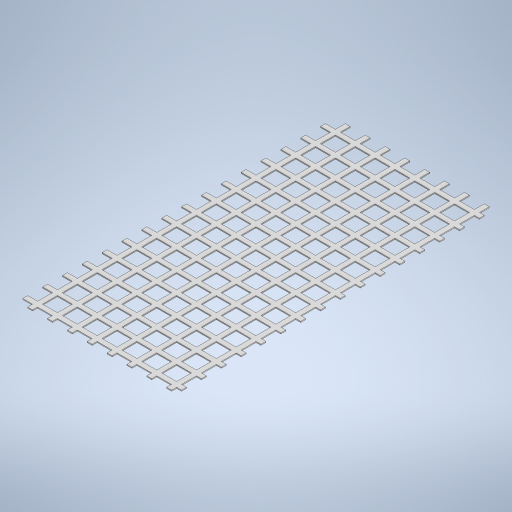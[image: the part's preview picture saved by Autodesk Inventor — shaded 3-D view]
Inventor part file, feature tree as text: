
AUTODESK INVENTOR PART (.ipt)
format: ipt  version: 2023 (Build 270158000, 158)  size: 695,296 bytes
history: native  units: in
note: dims shown in document units (in); Inventor stores cm internally (conversion verified against a paired STEP export)
features: extrude x2, pattern_linear x2, sketch x1
ambient origin geometry x8: Origin, YZ Plane, XZ Plane, XY Plane, X Axis, Y Axis, Z Axis, Center Point
bodies: Solid1 (feature_tree)
feature tree (5):
  sketch  "Sketch1"  dims[d0=54.0in d1=54.0in d2=1.0in d3=1.0in d4=8.0in d5=16.0in d6=8.0in d7=16.0in d8=16.0in d9=8.0in d10=16.0in d11=8.0in d12=4.0in d13=4.0in d14=4.0in d15=4.0in d16=17.0in d17=17.0in d18=17.0in d19=17.0in d20=20.0in d21=1.0in d22=1.0in d23=1.0in d24=1.0in d34=0.25in d35=0.25in d36=0.25in d37=0.25in d38=0.25in d39=0.25in d40=0.25in d41=0.25in d42=0.5in d43=0.25in d44=0.05in d45=0.0in d46=3.1496in d48=1.0in d49=0.5in d50=0.25in d51=0.05in d52=0.0in d53=6.2992in d55=1.0in d54=0.0344in]
  extrude  "Extrusion1"  Depth=1.0in
  pattern_linear  "Rectangular Pattern1"  Spacing1=1.0in  [1 undecoded]
  extrude  "Extrusion2"  Depth=1.0in
  pattern_linear  "Rectangular Pattern2"  Spacing1=8.0in  [1 undecoded]
note: 2 required parameter values undecoded (feature->parameter linkage not recoverable at this tier; creation-order binding heuristic only, values carry confidence <= 0.55)
